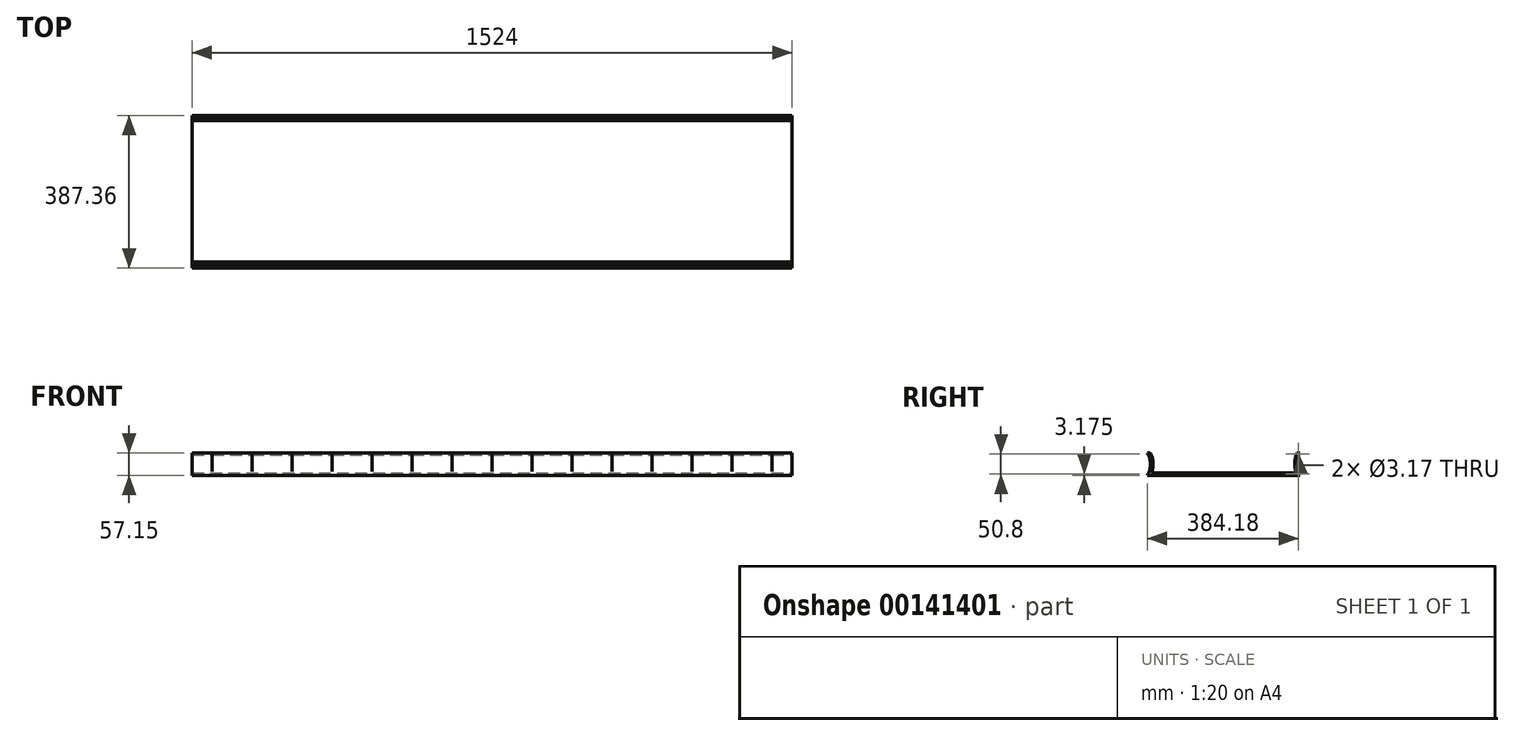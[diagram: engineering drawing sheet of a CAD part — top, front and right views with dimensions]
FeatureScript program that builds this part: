
annotation { "Feature Type Name" : "Feature", "Feature Type Description" : "" }
export const myFeature = defineFeature(function(context is Context, id is Id, definition is map)
    precondition{}
    {
        {
            var Q0;
            Q0=qCreatedBy(makeId("Right.planeOp"),FACE);
            var sketch = newSketch(context, id + "F0", { "sketchPlane" : qUnion([Q0])});
            skLineSegment(sketch, "E0", {"start": v(-193.68, 0) * mm, "end": v(193.68, 0) * mm});
            skArc(sketch, "E1", {"start": v(193.67, 57.15) * mm, "mid": v(187.56, 28.57) * mm, "end": v(193.68, 0) * mm});
            skArc(sketch, "E2", {"start": v(186.77, 57.15) * mm, "mid": v(181.29, 31.94) * mm, "end": v(184.53, 6.35) * mm});
            skLineSegment(sketch, "E3", {"start": v(184.53, 6.35) * mm, "end": v(-183.02, 6.35) * mm});
            skArc(sketch, "E4", {"start": v(-183.02, 6.35) * mm, "mid": v(-178.64, 32.12) * mm, "end": v(-186.18, 57.15) * mm});
            skArc(sketch, "E5", {"start": v(-193.68, 0) * mm, "mid": v(-184.88, 28.57) * mm, "end": v(-193.68, 57.15) * mm});
            skLineSegment(sketch, "E6", {"start": v(-193.68, 57.15) * mm, "end": v(-186.18, 57.15) * mm});
            skLineSegment(sketch, "E7", {"start": v(186.77, 57.15) * mm, "end": v(193.68, 57.15) * mm});
            skSolve(sketch);
        }
        {
            var Q0;
            Q0=qSketchRegion(id+"F0",true);
            extrude(context, id + "F1", {"entities" : qUnion([Q0]), "oppositeDirection" : true, "depth" : 1524 * mm});
        }
        {
            var Q0;
            Q0=makeQuery(id+"F1.opExtrude","CAP_FACE",FACE,{"disambiguationData":[OSD([sQuery(id+"F0.wireOp",EDGE,"E0"),sQuery(id+"F0.wireOp",EDGE,"E1"),sQuery(id+"F0.wireOp",EDGE,"E2"),sQuery(id+"F0.wireOp",EDGE,"E3"),sQuery(id+"F0.wireOp",EDGE,"E4"),sQuery(id+"F0.wireOp",EDGE,"E5"),sQuery(id+"F0.wireOp",EDGE,"E6"),sQuery(id+"F0.wireOp",EDGE,"E7")])],"isStart":true});
            var sketch = newSketch(context, id + "F2", { "sketchPlane" : qUnion([Q0])});
            skCircle(sketch, "E8", {"center": v(190.5, 53.97) * mm, "radius": 1.59 * mm});
            skCircle(sketch, "E9", {"center": v(190.5, 3.17) * mm, "radius": 1.59 * mm});
            skSolve(sketch);
        }
        {
            var Q0;
            Q0=qSketchRegion(id+"F2",true);
            extrude(context, id + "F3", {"entities" : qUnion([Q0]), "operationType" : NewBodyOperationType.REMOVE, "endBound" : BoundingType.THROUGH_ALL, "oppositeDirection" : true, "depth" : 25.4 * mm});
        }
        {
            var Q0;
            Q0=qCreatedBy(makeId("Front.planeOp"),FACE);
            var sketch = newSketch(context, id + "F4", { "sketchPlane" : qUnion([Q0])});
            skLineSegment(sketch, "E10.bottom", {"start": v(-50.8, 9.52) * mm, "end": v(-51.12, 9.52) * mm});
            skLineSegment(sketch, "E10.top", {"start": v(-50.8, 53.97) * mm, "end": v(-51.12, 53.97) * mm});
            skLineSegment(sketch, "E10.left", {"start": v(-50.8, 9.52) * mm, "end": v(-50.8, 53.97) * mm});
            skLineSegment(sketch, "E10.right", {"start": v(-51.12, 9.52) * mm, "end": v(-51.12, 53.97) * mm});
            skLineSegment(sketch, "E11.1.0.0", {"start": v(-152.4, 9.52) * mm, "end": v(-152.72, 9.52) * mm});
            skLineSegment(sketch, "E11.1.0.1", {"start": v(-152.72, 9.52) * mm, "end": v(-152.72, 53.97) * mm});
            skLineSegment(sketch, "E11.1.0.2", {"start": v(-152.4, 9.52) * mm, "end": v(-152.4, 53.97) * mm});
            skLineSegment(sketch, "E11.1.0.3", {"start": v(-152.4, 53.97) * mm, "end": v(-152.72, 53.97) * mm});
            skLineSegment(sketch, "E11.2.0.0", {"start": v(-254, 9.52) * mm, "end": v(-254.32, 9.52) * mm});
            skLineSegment(sketch, "E11.2.0.1", {"start": v(-254.32, 9.52) * mm, "end": v(-254.32, 53.97) * mm});
            skLineSegment(sketch, "E11.2.0.2", {"start": v(-254, 9.52) * mm, "end": v(-254, 53.97) * mm});
            skLineSegment(sketch, "E11.2.0.3", {"start": v(-254, 53.97) * mm, "end": v(-254.32, 53.97) * mm});
            skLineSegment(sketch, "E11.3.0.0", {"start": v(-355.6, 9.52) * mm, "end": v(-355.92, 9.52) * mm});
            skLineSegment(sketch, "E11.3.0.1", {"start": v(-355.92, 9.52) * mm, "end": v(-355.92, 53.97) * mm});
            skLineSegment(sketch, "E11.3.0.2", {"start": v(-355.6, 9.52) * mm, "end": v(-355.6, 53.97) * mm});
            skLineSegment(sketch, "E11.3.0.3", {"start": v(-355.6, 53.97) * mm, "end": v(-355.92, 53.97) * mm});
            skLineSegment(sketch, "E11.4.0.0", {"start": v(-457.2, 9.52) * mm, "end": v(-457.52, 9.52) * mm});
            skLineSegment(sketch, "E11.4.0.1", {"start": v(-457.52, 9.52) * mm, "end": v(-457.52, 53.97) * mm});
            skLineSegment(sketch, "E11.4.0.2", {"start": v(-457.2, 9.52) * mm, "end": v(-457.2, 53.97) * mm});
            skLineSegment(sketch, "E11.4.0.3", {"start": v(-457.2, 53.97) * mm, "end": v(-457.52, 53.97) * mm});
            skLineSegment(sketch, "E11.5.0.0", {"start": v(-558.8, 9.52) * mm, "end": v(-559.12, 9.52) * mm});
            skLineSegment(sketch, "E11.5.0.1", {"start": v(-559.12, 9.52) * mm, "end": v(-559.12, 53.97) * mm});
            skLineSegment(sketch, "E11.5.0.2", {"start": v(-558.8, 9.52) * mm, "end": v(-558.8, 53.97) * mm});
            skLineSegment(sketch, "E11.5.0.3", {"start": v(-558.8, 53.97) * mm, "end": v(-559.12, 53.97) * mm});
            skLineSegment(sketch, "E11.6.0.0", {"start": v(-660.4, 9.52) * mm, "end": v(-660.72, 9.52) * mm});
            skLineSegment(sketch, "E11.6.0.1", {"start": v(-660.72, 9.52) * mm, "end": v(-660.72, 53.97) * mm});
            skLineSegment(sketch, "E11.6.0.2", {"start": v(-660.4, 9.52) * mm, "end": v(-660.4, 53.97) * mm});
            skLineSegment(sketch, "E11.6.0.3", {"start": v(-660.4, 53.97) * mm, "end": v(-660.72, 53.97) * mm});
            skLineSegment(sketch, "E11.7.0.0", {"start": v(-762, 9.52) * mm, "end": v(-762.32, 9.52) * mm});
            skLineSegment(sketch, "E11.7.0.1", {"start": v(-762.32, 9.52) * mm, "end": v(-762.32, 53.97) * mm});
            skLineSegment(sketch, "E11.7.0.2", {"start": v(-762, 9.52) * mm, "end": v(-762, 53.97) * mm});
            skLineSegment(sketch, "E11.7.0.3", {"start": v(-762, 53.97) * mm, "end": v(-762.32, 53.97) * mm});
            skLineSegment(sketch, "E11.8.0.0", {"start": v(-863.6, 9.52) * mm, "end": v(-863.92, 9.52) * mm});
            skLineSegment(sketch, "E11.8.0.1", {"start": v(-863.92, 9.52) * mm, "end": v(-863.92, 53.97) * mm});
            skLineSegment(sketch, "E11.8.0.2", {"start": v(-863.6, 9.52) * mm, "end": v(-863.6, 53.97) * mm});
            skLineSegment(sketch, "E11.8.0.3", {"start": v(-863.6, 53.97) * mm, "end": v(-863.92, 53.97) * mm});
            skLineSegment(sketch, "E11.9.0.0", {"start": v(-965.2, 9.52) * mm, "end": v(-965.52, 9.52) * mm});
            skLineSegment(sketch, "E11.9.0.1", {"start": v(-965.52, 9.52) * mm, "end": v(-965.52, 53.97) * mm});
            skLineSegment(sketch, "E11.9.0.2", {"start": v(-965.2, 9.52) * mm, "end": v(-965.2, 53.97) * mm});
            skLineSegment(sketch, "E11.9.0.3", {"start": v(-965.2, 53.97) * mm, "end": v(-965.52, 53.97) * mm});
            skLineSegment(sketch, "E11.10.0.0", {"start": v(-1066.8, 9.52) * mm, "end": v(-1067.12, 9.52) * mm});
            skLineSegment(sketch, "E11.10.0.1", {"start": v(-1067.12, 9.52) * mm, "end": v(-1067.12, 53.97) * mm});
            skLineSegment(sketch, "E11.10.0.2", {"start": v(-1066.8, 9.52) * mm, "end": v(-1066.8, 53.97) * mm});
            skLineSegment(sketch, "E11.10.0.3", {"start": v(-1066.8, 53.97) * mm, "end": v(-1067.12, 53.97) * mm});
            skLineSegment(sketch, "E11.11.0.0", {"start": v(-1168.4, 9.52) * mm, "end": v(-1168.72, 9.52) * mm});
            skLineSegment(sketch, "E11.11.0.1", {"start": v(-1168.72, 9.52) * mm, "end": v(-1168.72, 53.97) * mm});
            skLineSegment(sketch, "E11.11.0.2", {"start": v(-1168.4, 9.52) * mm, "end": v(-1168.4, 53.97) * mm});
            skLineSegment(sketch, "E11.11.0.3", {"start": v(-1168.4, 53.97) * mm, "end": v(-1168.72, 53.97) * mm});
            skLineSegment(sketch, "E11.direction1", {"start": v(-51.12, 9.52) * mm, "end": v(-152.72, 9.52) * mm, "construction": true});
            skLineSegment(sketch, "E12.0.12.0", {"start": v(-1270, 9.52) * mm, "end": v(-1270.32, 9.52) * mm});
            skLineSegment(sketch, "E12.3.12.0", {"start": v(-1270.32, 9.52) * mm, "end": v(-1270.32, 53.97) * mm});
            skLineSegment(sketch, "E12.6.12.0", {"start": v(-1270, 9.52) * mm, "end": v(-1270, 53.97) * mm});
            skLineSegment(sketch, "E12.9.12.0", {"start": v(-1270, 53.97) * mm, "end": v(-1270.32, 53.97) * mm});
            skLineSegment(sketch, "E12.0.13.0", {"start": v(-1371.6, 9.52) * mm, "end": v(-1371.92, 9.52) * mm});
            skLineSegment(sketch, "E12.3.13.0", {"start": v(-1371.92, 9.52) * mm, "end": v(-1371.92, 53.97) * mm});
            skLineSegment(sketch, "E12.6.13.0", {"start": v(-1371.6, 9.52) * mm, "end": v(-1371.6, 53.97) * mm});
            skLineSegment(sketch, "E12.9.13.0", {"start": v(-1371.6, 53.97) * mm, "end": v(-1371.92, 53.97) * mm});
            skLineSegment(sketch, "E12.0.14.0", {"start": v(-1473.2, 9.52) * mm, "end": v(-1473.52, 9.52) * mm});
            skLineSegment(sketch, "E12.3.14.0", {"start": v(-1473.52, 9.52) * mm, "end": v(-1473.52, 53.97) * mm});
            skLineSegment(sketch, "E12.6.14.0", {"start": v(-1473.2, 9.52) * mm, "end": v(-1473.2, 53.97) * mm});
            skLineSegment(sketch, "E12.9.14.0", {"start": v(-1473.2, 53.97) * mm, "end": v(-1473.52, 53.97) * mm});
            skSolve(sketch);
        }
        {
            var Q0;
            Q0=qSketchRegion(id+"F4",true);
            var Q1;
            Q1=makeQuery(id+"F1.opExtrude","SWEPT_FACE",FACE,{"disambiguationData":[OSD([sQuery(id+"F0.wireOp",EDGE,"E1")])]});
            var Q2;
            Q2=makeQuery(id+"F1.opExtrude","SWEPT_FACE",FACE,{"disambiguationData":[OSD([sQuery(id+"F0.wireOp",EDGE,"E5")])]});
            extrude(context, id + "F5", {"entities" : qUnion([Q0]), "operationType" : NewBodyOperationType.REMOVE, "endBound" : BoundingType.UP_TO_SURFACE, "oppositeDirection" : true, "endBoundEntityFace" : qUnion([Q1]), "depth" : 25.4 * mm, "hasSecondDirection" : true, "secondDirectionBound" : BoundingType.UP_TO_SURFACE, "secondDirectionOppositeDirection" : false, "secondDirectionBoundEntityFace" : qUnion([Q2]), "secondDirectionDepth" : 25.4 * mm});
        }
    });
